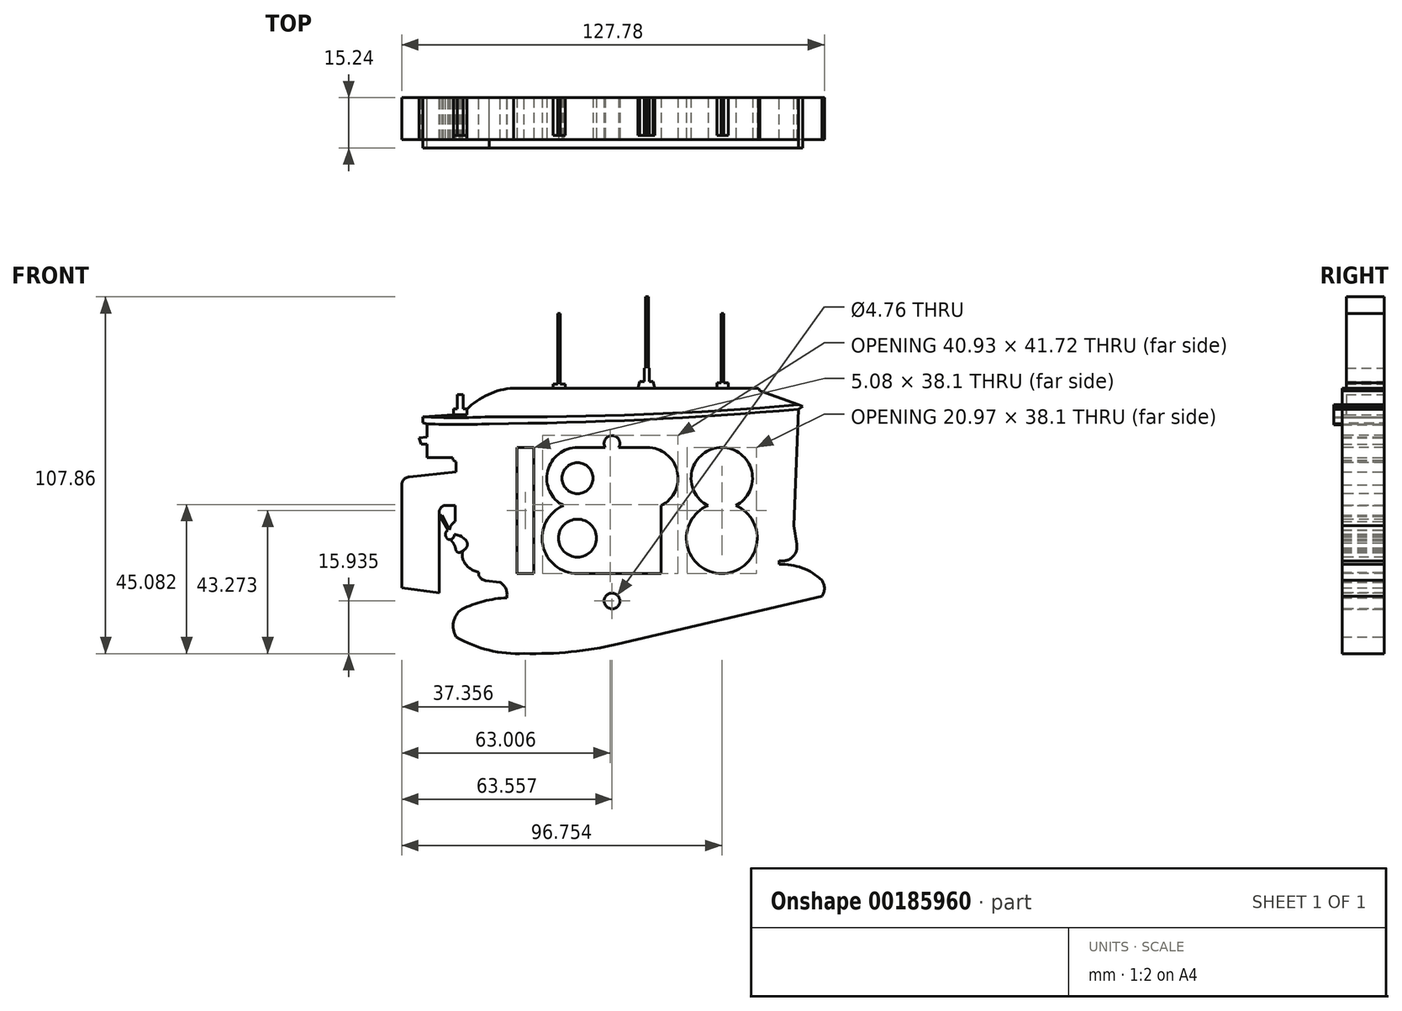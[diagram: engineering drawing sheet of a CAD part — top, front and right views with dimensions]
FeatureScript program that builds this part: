
annotation { "Feature Type Name" : "Feature", "Feature Type Description" : "" }
export const myFeature = defineFeature(function(context is Context, id is Id, definition is map)
    precondition{}
    {
        {
            var Q0;
            Q0=qCreatedBy(makeId("Front.planeOp"),FACE);
            var sketch = newSketch(context, id + "F0", { "sketchPlane" : qUnion([Q0])});
            skLineSegment(sketch, "E0", {"start": v(-48.76, 13.42) * mm, "end": v(-62.86, 11.96) * mm});
            skArc(sketch, "E1", {"start": v(-62.86, 11.96) * mm, "mid": v(-64.46, 11.17) * mm, "end": v(-65.16, 9.53) * mm});
            skLineSegment(sketch, "E2", {"start": v(-65.16, 9.53) * mm, "end": v(-65.16, -21.6) * mm});
            skLineSegment(sketch, "E3", {"start": v(-65.16, -21.6) * mm, "end": v(-53.86, -23.17) * mm});
            skLineSegment(sketch, "E4", {"start": v(-53.86, -23.17) * mm, "end": v(-53.86, 1.02) * mm});
            skArc(sketch, "E5", {"start": v(-52.52, 3.2) * mm, "mid": v(-53.5, 2.3) * mm, "end": v(-53.86, 1.02) * mm});
            skLineSegment(sketch, "E6", {"start": v(-52.52, 3.2) * mm, "end": v(-49.04, 3.2) * mm});
            skLineSegment(sketch, "E7", {"start": v(-48.76, 13.42) * mm, "end": v(-48.76, 16.5) * mm});
            skLineSegment(sketch, "E8", {"start": v(-48.76, 16.5) * mm, "end": v(-49.66, 16.94) * mm});
            skLineSegment(sketch, "E9", {"start": v(-49.66, 16.94) * mm, "end": v(-49.74, 17.72) * mm});
            skLineSegment(sketch, "E10", {"start": v(-49.74, 17.72) * mm, "end": v(-57.46, 17.72) * mm});
            skLineSegment(sketch, "E11", {"start": v(-57.46, 17.72) * mm, "end": v(-57.46, 21.86) * mm});
            skLineSegment(sketch, "E12", {"start": v(-57.46, 21.86) * mm, "end": v(-59.24, 21.86) * mm});
            skLineSegment(sketch, "E13", {"start": v(-59.24, 21.86) * mm, "end": v(-59.95, 23.65) * mm});
            skLineSegment(sketch, "E14", {"start": v(-59.95, 23.65) * mm, "end": v(-57.48, 23.9) * mm});
            skLineSegment(sketch, "E15", {"start": v(-57.48, 23.9) * mm, "end": v(-57.48, 27.94) * mm});
            skLineSegment(sketch, "E16", {"start": v(-57.48, 27.94) * mm, "end": v(-58.72, 28.29) * mm});
            skLineSegment(sketch, "E17", {"start": v(-58.72, 28.29) * mm, "end": v(-58.72, 30.1) * mm});
            skLineSegment(sketch, "E18", {"start": v(-58.72, 30.1) * mm, "end": v(-49.56, 30.65) * mm});
            skLineSegment(sketch, "E19", {"start": v(-49.56, 30.65) * mm, "end": v(-49.56, 32.46) * mm});
            skLineSegment(sketch, "E20", {"start": v(-49.56, 32.46) * mm, "end": v(-48.32, 32.46) * mm});
            skLineSegment(sketch, "E21", {"start": v(-48.32, 32.46) * mm, "end": v(-48.32, 36.74) * mm});
            skLineSegment(sketch, "E22", {"start": v(-48.32, 36.74) * mm, "end": v(-46.61, 36.74) * mm});
            skLineSegment(sketch, "E23", {"start": v(-46.61, 36.74) * mm, "end": v(-46.61, 32.46) * mm});
            skLineSegment(sketch, "E24", {"start": v(-46.61, 32.46) * mm, "end": v(-45.47, 32.46) * mm});
            skLineSegment(sketch, "E25", {"start": v(-45.47, 32.46) * mm, "end": v(-45.47, 32.32) * mm});
            skArc(sketch, "E26", {"start": v(-31.38, 38.73) * mm, "mid": v(-39.02, 36.84) * mm, "end": v(-45.47, 32.32) * mm});
            skLineSegment(sketch, "E27", {"start": v(-31.38, 38.73) * mm, "end": v(42.69, 38.73) * mm});
            skLineSegment(sketch, "E28", {"start": v(42.69, 38.73) * mm, "end": v(43.05, 37.94) * mm});
            skLineSegment(sketch, "E29", {"start": v(43.05, 37.94) * mm, "end": v(56.03, 33.26) * mm});
            skLineSegment(sketch, "E30", {"start": v(56.03, 33.26) * mm, "end": v(54.75, 32.34) * mm});
            skLineSegment(sketch, "E31", {"start": v(54.75, 32.34) * mm, "end": v(53.41, -2.84) * mm});
            skLineSegment(sketch, "E32", {"start": v(53.41, -2.84) * mm, "end": v(54.27, -8.48) * mm});
            skArc(sketch, "E33", {"start": v(48.95, -13.4) * mm, "mid": v(52.92, -12.35) * mm, "end": v(54.27, -8.48) * mm});
            skLineSegment(sketch, "E34", {"start": v(48.95, -13.4) * mm, "end": v(48.95, -14.57) * mm});
            skArc(sketch, "E35", {"start": v(61.84, -19.38) * mm, "mid": v(55.9, -15.63) * mm, "end": v(48.95, -14.57) * mm});
            skArc(sketch, "E36", {"start": v(61.84, -24.22) * mm, "mid": v(62.62, -21.8) * mm, "end": v(61.84, -19.38) * mm});
            skLineSegment(sketch, "E37", {"start": v(61.84, -24.22) * mm, "end": v(0, -38.68) * mm});
            skArc(sketch, "E38", {"start": v(-28.17, -41.47) * mm, "mid": v(-14, -41) * mm, "end": v(0, -38.68) * mm});
            skArc(sketch, "E39", {"start": v(-48.72, -36.43) * mm, "mid": v(-38.82, -40.48) * mm, "end": v(-28.17, -41.47) * mm});
            skArc(sketch, "E40", {"start": v(-47.02, -28.16) * mm, "mid": v(-49.5, -31.96) * mm, "end": v(-48.72, -36.43) * mm});
            skArc(sketch, "E41", {"start": v(-33.4, -24.65) * mm, "mid": v(-40.4, -25.7) * mm, "end": v(-47.02, -28.16) * mm});
            skArc(sketch, "E42", {"start": v(-33.4, -24.65) * mm, "mid": v(-33.66, -21.98) * mm, "end": v(-35.39, -19.93) * mm});
            skLineSegment(sketch, "E43", {"start": v(-35.39, -19.93) * mm, "end": v(-39.85, -19.43) * mm});
            skArc(sketch, "E44", {"start": v(-41.93, -16.91) * mm, "mid": v(-41.4, -18.6) * mm, "end": v(-39.85, -19.43) * mm});
            skArc(sketch, "E45", {"start": v(-46.6, -13.2) * mm, "mid": v(-44.71, -15.62) * mm, "end": v(-41.93, -16.91) * mm});
            skArc(sketch, "E46", {"start": v(-46.6, -10.27) * mm, "mid": v(-46.84, -11.74) * mm, "end": v(-46.6, -13.2) * mm});
            skArc(sketch, "E47", {"start": v(-46.6, -10.27) * mm, "mid": v(-45.82, -8.68) * mm, "end": v(-46.36, -6.99) * mm});
            skLineSegment(sketch, "E48", {"start": v(-49.04, 3.2) * mm, "end": v(-49.04, -1.54) * mm});
            skArc(sketch, "E49", {"start": v(-49.04, -1.54) * mm, "mid": v(-50.85, -5.02) * mm, "end": v(-49.04, -8.5) * mm});
            skArc(sketch, "E50", {"start": v(-49.04, -8.5) * mm, "mid": v(-47.3, -5.02) * mm, "end": v(-49.04, -1.54) * mm});
            skLineSegment(sketch, "E51", {"start": v(-46.36, -6.99) * mm, "end": v(-47.37, -5.75) * mm});
            skArc(sketch, "E52", {"start": v(-50.74, -4.05) * mm, "mid": v(-51.6, -4.53) * mm, "end": v(-51.97, -5.43) * mm});
            skArc(sketch, "E53", {"start": v(-51.97, -5.43) * mm, "mid": v(-51.73, -6.26) * mm, "end": v(-51.19, -6.94) * mm});
            skArc(sketch, "E54", {"start": v(-51.19, -6.94) * mm, "mid": v(-50.77, -7.02) * mm, "end": v(-50.35, -7.02) * mm});
            skArc(sketch, "E55", {"start": v(-50.35, -7.02) * mm, "mid": v(-49.27, -5.37) * mm, "end": v(-50.74, -4.05) * mm});
            skArc(sketch, "E56", {"start": v(-45.65, -7.36) * mm, "mid": v(-47.84, -5.85) * mm, "end": v(-50.48, -5.52) * mm});
            skArc(sketch, "E57", {"start": v(-45.65, -9.55) * mm, "mid": v(-45.29, -8.46) * mm, "end": v(-45.65, -7.36) * mm});
            skArc(sketch, "E58", {"start": v(-47.7, -11) * mm, "mid": v(-46.59, -10.39) * mm, "end": v(-45.65, -9.55) * mm});
            skArc(sketch, "E59", {"start": v(-48.83, -10.03) * mm, "mid": v(-48.44, -10.73) * mm, "end": v(-47.7, -11) * mm});
            skArc(sketch, "E60", {"start": v(-48.83, -10.03) * mm, "mid": v(-49.38, -8.42) * mm, "end": v(-50.35, -7.02) * mm});
            skArc(sketch, "E61", {"start": v(-57.48, 27.94) * mm, "mid": v(-48.1, 27.7) * mm, "end": v(-38.7, 27.94) * mm});
            skArc(sketch, "E62", {"start": v(-38.7, 27.94) * mm, "mid": v(8.07, 29.23) * mm, "end": v(54.75, 32.34) * mm});
            skLineSegment(sketch, "E63", {"start": v(-33.4, -24.65) * mm, "end": v(-33.4, -29.1) * mm});
            skLineSegment(sketch, "E64", {"start": v(-33.4, -29.1) * mm, "end": v(-28.45, -28) * mm});
            skLineSegment(sketch, "E65", {"start": v(-28.45, -28) * mm, "end": v(-28.45, -31.15) * mm});
            skLineSegment(sketch, "E66", {"start": v(-28.45, -31.15) * mm, "end": v(-16.41, -28.65) * mm});
            skLineSegment(sketch, "E67", {"start": v(-16.41, -28.65) * mm, "end": v(-17.59, -27.26) * mm});
            skLineSegment(sketch, "E68", {"start": v(-17.59, -27.26) * mm, "end": v(0, -33.2) * mm});
            skLineSegment(sketch, "E69", {"start": v(0, -33.2) * mm, "end": v(6.99, -31.66) * mm});
            skLineSegment(sketch, "E70", {"start": v(6.99, -31.66) * mm, "end": v(6.99, -12.15) * mm});
            skLineSegment(sketch, "E71", {"start": v(6.99, -12.15) * mm, "end": v(44.04, -6.2) * mm});
            skLineSegment(sketch, "E72", {"start": v(44.04, -6.2) * mm, "end": v(44.04, -23.6) * mm});
            skLineSegment(sketch, "E73", {"start": v(44.04, -23.6) * mm, "end": v(48.95, -22.5) * mm});
            skLineSegment(sketch, "E74", {"start": v(48.95, -22.5) * mm, "end": v(48.95, -14.57) * mm});
            skLineSegment(sketch, "E75", {"start": v(0, -33.2) * mm, "end": v(0, -6.11) * mm});
            skLineSegment(sketch, "E76", {"start": v(0, -6.11) * mm, "end": v(48.68, 1.7) * mm});
            skLineSegment(sketch, "E77", {"start": v(48.68, 1.7) * mm, "end": v(48.95, -13.4) * mm});
            skLineSegment(sketch, "E78", {"start": v(0, -6.11) * mm, "end": v(-5.2, -5.38) * mm});
            skLineSegment(sketch, "E79", {"start": v(-5.2, -5.38) * mm, "end": v(38.9, 1.7) * mm});
            skLineSegment(sketch, "E80", {"start": v(38.9, 1.7) * mm, "end": v(48.68, 1.7) * mm});
            skLineSegment(sketch, "E81", {"start": v(-5.2, -5.38) * mm, "end": v(-5.2, -31.45) * mm});
            skArc(sketch, "E82", {"start": v(-15.78, -17.4) * mm, "mid": v(-8.22, -13.39) * mm, "end": v(-5.2, -5.38) * mm});
            skArc(sketch, "E83", {"start": v(-35.39, -19.93) * mm, "mid": v(-25.56, -18.86) * mm, "end": v(-15.78, -17.4) * mm});
            skArc(sketch, "E84", {"start": v(-58.72, 30.1) * mm, "mid": v(-48.71, 29.82) * mm, "end": v(-38.7, 30.1) * mm});
            skArc(sketch, "E85", {"start": v(-38.7, 30.1) * mm, "mid": v(8.07, 30.8) * mm, "end": v(54.75, 33.72) * mm});
            skLineSegment(sketch, "E86", {"start": v(-19.35, 38.73) * mm, "end": v(-19.35, 39.97) * mm});
            skLineSegment(sketch, "E87", {"start": v(-19.35, 39.97) * mm, "end": v(-15.67, 39.97) * mm});
            skLineSegment(sketch, "E88", {"start": v(-15.67, 39.97) * mm, "end": v(-15.67, 38.73) * mm});
            skLineSegment(sketch, "E89", {"start": v(-18.02, 39.97) * mm, "end": v(-18.02, 61.27) * mm});
            skLineSegment(sketch, "E90", {"start": v(-18.02, 61.27) * mm, "end": v(-17.22, 61.27) * mm});
            skLineSegment(sketch, "E91", {"start": v(-17.22, 61.27) * mm, "end": v(-17.22, 39.97) * mm});
            skLineSegment(sketch, "E92", {"start": v(30.18, 38.73) * mm, "end": v(30.18, 40.4) * mm});
            skLineSegment(sketch, "E93", {"start": v(30.18, 40.4) * mm, "end": v(33.56, 40.4) * mm});
            skLineSegment(sketch, "E94", {"start": v(33.56, 40.4) * mm, "end": v(33.56, 38.73) * mm});
            skLineSegment(sketch, "E95", {"start": v(31.4, 40.4) * mm, "end": v(31.4, 61.27) * mm});
            skLineSegment(sketch, "E96", {"start": v(31.4, 61.27) * mm, "end": v(32.2, 61.27) * mm});
            skLineSegment(sketch, "E97", {"start": v(32.2, 61.27) * mm, "end": v(32.2, 40.4) * mm});
            skLineSegment(sketch, "E98", {"start": v(6.24, 38.73) * mm, "end": v(6.79, 40.79) * mm});
            skLineSegment(sketch, "E99", {"start": v(6.79, 40.79) * mm, "end": v(8.11, 40.79) * mm});
            skLineSegment(sketch, "E100", {"start": v(8.11, 40.79) * mm, "end": v(8.11, 44.74) * mm});
            skLineSegment(sketch, "E101", {"start": v(8.11, 44.74) * mm, "end": v(9.64, 44.74) * mm});
            skLineSegment(sketch, "E102", {"start": v(9.64, 44.74) * mm, "end": v(9.64, 40.79) * mm});
            skLineSegment(sketch, "E103", {"start": v(9.64, 40.79) * mm, "end": v(10.8, 40.79) * mm});
            skLineSegment(sketch, "E104", {"start": v(10.8, 40.79) * mm, "end": v(11.36, 38.73) * mm});
            skLineSegment(sketch, "E105", {"start": v(8.57, 44.74) * mm, "end": v(8.57, 66.33) * mm});
            skLineSegment(sketch, "E106", {"start": v(8.57, 66.33) * mm, "end": v(9.38, 66.33) * mm});
            skLineSegment(sketch, "E107", {"start": v(9.38, 66.33) * mm, "end": v(9.38, 44.74) * mm});
            skLineSegment(sketch, "E108", {"start": v(6.99, -31.66) * mm, "end": v(44.04, -23.6) * mm});
            skArc(sketch, "E109", {"start": v(-28.12, -36.29) * mm, "mid": v(-13.98, -35.5) * mm, "end": v(0, -33.2) * mm});
            skArc(sketch, "E110", {"start": v(-45.38, -33.2) * mm, "mid": v(-36.97, -35.96) * mm, "end": v(-28.12, -36.29) * mm});
            skArc(sketch, "E111", {"start": v(-47.02, -28.16) * mm, "mid": v(-46.99, -30.94) * mm, "end": v(-45.38, -33.2) * mm});
            skLineSegment(sketch, "E112", {"start": v(-49.56, 30.65) * mm, "end": v(-45.47, 30.65) * mm});
            skLineSegment(sketch, "E113", {"start": v(-45.47, 30.65) * mm, "end": v(-45.47, 32.32) * mm});
            skLineSegment(sketch, "E114", {"start": v(-51.2, -4.22) * mm, "end": v(-53.6, -0.05) * mm});
            skLineSegment(sketch, "E115", {"start": v(-53.6, -0.05) * mm, "end": v(-52.96, 0.32) * mm});
            skLineSegment(sketch, "E116", {"start": v(-52.96, 0.32) * mm, "end": v(-50.74, -4.05) * mm});
            skSolve(sketch);
        }
        {
            var Q0;
            Q0=makeQuery(id+"F0.imprint","IMPRINT",FACE,{"disambiguationData":[TD([[makeQuery(id+"F0.imprint","IMPRINT",EDGE,{"derivedFrom":sQuery(id+"F0.wireOp",EDGE,"E0")}),1.0]])]});
            var Q1;
            {var subQ5=sQuery(id+"F0.wireOp",EDGE,"E50");var subQ7=makeQuery(id+"F0.imprint","INTERSECT",VERTEX,{"derivedFrom":[subQ5,sQuery(id+"F0.wireOp",EDGE,"E51")]});Q1=makeQuery(id+"F0.imprint","IMPRINT",FACE,{"disambiguationData":[TD([[makeQuery(id+"F0.imprint","IMPRINT",EDGE,{"disambiguationData":[TD([[subQ7,1.0]])],"derivedFrom":subQ5}),1.0]])]});}
            var Q2;
            {var subQ0=sQuery(id+"F0.wireOp",EDGE,"E53");Q2=makeQuery(id+"F0.imprint","IMPRINT",FACE,{"disambiguationData":[TD([[makeQuery(id+"F0.imprint","IMPRINT",EDGE,{"derivedFrom":subQ0}),1.0]])]});}
            var Q3;
            {var subQ1=sQuery(id+"F0.wireOp",EDGE,"E49");var subQ3=makeQuery(id+"F0.imprint","INTERSECT",VERTEX,{"derivedFrom":[subQ1,sQuery(id+"F0.wireOp",EDGE,"JAnZBrHo-FBBG-eloX-0JCn-rR0iuovSbzPm")]});Q3=makeQuery(id+"F0.imprint","IMPRINT",FACE,{"disambiguationData":[TD([[makeQuery(id+"F0.imprint","IMPRINT",EDGE,{"disambiguationData":[TD([[subQ3,1.0]])],"derivedFrom":subQ1}),1.0]])]});}
            var Q4;
            Q4=makeQuery(id+"F0.imprint","IMPRINT",FACE,{"disambiguationData":[TD([[makeQuery(id+"F0.imprint","IMPRINT",EDGE,{"derivedFrom":sQuery(id+"F0.wireOp",EDGE,"E41")}),1.0]])]});
            var Q5;
            Q5=makeQuery(id+"F0.imprint","IMPRINT",FACE,{"disambiguationData":[TD([[makeQuery(id+"F0.imprint","IMPRINT",EDGE,{"derivedFrom":sQuery(id+"F0.wireOp",EDGE,"E35")}),1.0]])]});
            var Q6;
            Q6=makeQuery(id+"F0.imprint","IMPRINT",FACE,{"disambiguationData":[TD([[makeQuery(id+"F0.imprint","IMPRINT",EDGE,{"derivedFrom":sQuery(id+"F0.wireOp",EDGE,"E42")}),-1.0]])]});
            var Q7;
            Q7=makeQuery(id+"F0.imprint","IMPRINT",FACE,{"disambiguationData":[TD([[makeQuery(id+"F0.imprint","IMPRINT",EDGE,{"derivedFrom":sQuery(id+"F0.wireOp",EDGE,"E70")}),-1.0]])]});
            var Q8;
            Q8=makeQuery(id+"F0.imprint","IMPRINT",FACE,{"disambiguationData":[TD([[makeQuery(id+"F0.imprint","IMPRINT",EDGE,{"derivedFrom":sQuery(id+"F0.wireOp",EDGE,"E18")}),-1.0]])]});
            var Q9;
            Q9=makeQuery(id+"F0.imprint","IMPRINT",FACE,{"disambiguationData":[TD([[makeQuery(id+"F0.imprint","IMPRINT",EDGE,{"derivedFrom":sQuery(id+"F0.wireOp",EDGE,"E34")}),-1.0]])]});
            var Q10;
            Q10=makeQuery(id+"F0.imprint","IMPRINT",FACE,{"disambiguationData":[TD([[makeQuery(id+"F0.imprint","IMPRINT",EDGE,{"derivedFrom":sQuery(id+"F0.wireOp",EDGE,"E76")}),1.0]])]});
            var Q11;
            {var subQ0=sQuery(id+"F0.wireOp",EDGE,"E75");Q11=makeQuery(id+"F0.imprint","IMPRINT",FACE,{"disambiguationData":[TD([[makeQuery(id+"F0.imprint","IMPRINT",EDGE,{"derivedFrom":subQ0}),1.0]])]});}
            var Q12;
            {var subQ0=sQuery(id+"F0.wireOp",EDGE,"E55");var subQ4=makeQuery(id+"F0.imprint","INTERSECT",VERTEX,{"derivedFrom":[subQ0,sQuery(id+"F0.wireOp",EDGE,"E56")]});Q12=makeQuery(id+"F0.imprint","IMPRINT",FACE,{"disambiguationData":[TD([[makeQuery(id+"F0.imprint","IMPRINT",EDGE,{"disambiguationData":[TD([[subQ4,1.0]])],"derivedFrom":subQ0}),1.0]])]});}
            var Q13;
            {var subQ2=sQuery(id+"F0.wireOp",EDGE,"E114");Q13=makeQuery(id+"F0.imprint","IMPRINT",FACE,{"disambiguationData":[TD([[makeQuery(id+"F0.imprint","IMPRINT",EDGE,{"derivedFrom":subQ2}),-1.0]])]});}
            var Q14;
            {var subQ2=sQuery(id+"F0.wireOp",EDGE,"E49");var subQ6=sQuery(id+"F0.wireOp",EDGE,"E50");var subQ7=makeQuery(id+"F0.imprint","INTERSECT",VERTEX,{"derivedFrom":[subQ2,subQ6]});Q14=makeQuery(id+"F0.imprint","IMPRINT",FACE,{"disambiguationData":[TD([[makeQuery(id+"F0.imprint","IMPRINT",EDGE,{"disambiguationData":[TD([[subQ7,1.0]])],"derivedFrom":subQ2}),1.0]])]});}
            var Q15;
            {var subQ8=sQuery(id+"F0.wireOp",EDGE,"E47");Q15=makeQuery(id+"F0.imprint","IMPRINT",FACE,{"disambiguationData":[TD([[makeQuery(id+"F0.imprint","IMPRINT",EDGE,{"derivedFrom":subQ8}),1.0]])]});}
            var Q16;
            {var subQ4=sQuery(id+"F0.wireOp",EDGE,"E47");Q16=makeQuery(id+"F0.imprint","IMPRINT",FACE,{"disambiguationData":[TD([[makeQuery(id+"F0.imprint","IMPRINT",EDGE,{"derivedFrom":subQ4}),-1.0]])]});}
            var Q17;
            {var subQ0=sQuery(id+"F0.wireOp",EDGE,"E51");var subQ1=sQuery(id+"F0.wireOp",EDGE,"E50");var subQ2=makeQuery(id+"F0.imprint","INTERSECT",VERTEX,{"derivedFrom":[subQ1,subQ0]});Q17=makeQuery(id+"F0.imprint","IMPRINT",FACE,{"disambiguationData":[TD([[makeQuery(id+"F0.imprint","IMPRINT",EDGE,{"disambiguationData":[TD([[subQ2,1.0]])],"derivedFrom":subQ1}),-1.0]])]});}
            extrude(context, id + "F1", {"entities" : qUnion([Q0, Q1, Q2, Q3, Q4, Q5, Q6, Q7, Q8, Q9, Q10, Q11, Q12, Q13, Q14, Q15, Q16, Q17]), "depth" : 12.7 * mm});
        }
        {
            var Q0;
            {var subQ5=sQuery(id+"F0.wireOp",EDGE,"E47");Q0=makeQuery(id+"F0.imprint","IMPRINT",FACE,{"disambiguationData":[TD([[makeQuery(id+"F0.imprint","IMPRINT",EDGE,{"derivedFrom":subQ5}),1.0]])]});}
            var Q1;
            {var subQ3=sQuery(id+"F0.wireOp",EDGE,"E50");var subQ6=sQuery(id+"F0.wireOp",EDGE,"E49");var subQ8=makeQuery(id+"F0.imprint","INTERSECT",VERTEX,{"derivedFrom":[subQ6,subQ3]});Q1=makeQuery(id+"F0.imprint","IMPRINT",FACE,{"disambiguationData":[TD([[makeQuery(id+"F0.imprint","IMPRINT",EDGE,{"disambiguationData":[TD([[subQ8,1.0]])],"derivedFrom":subQ6}),1.0]])]});}
            var Q2;
            {var subQ0=sQuery(id+"F0.wireOp",EDGE,"wI7tyHVv-ab6v-So0j-KQO8-YM4SJzSUTnYV");Q2=makeQuery(id+"F0.imprint","IMPRINT",FACE,{"disambiguationData":[TD([[makeQuery(id+"F0.imprint","IMPRINT",EDGE,{"derivedFrom":subQ0}),1.0]])]});}
            var Q3;
            {var subQ1=sQuery(id+"F0.wireOp",EDGE,"E49");var subQ3=sQuery(id+"F0.wireOp",EDGE,"JAnZBrHo-FBBG-eloX-0JCn-rR0iuovSbzPm");var subQ4=makeQuery(id+"F0.imprint","INTERSECT",VERTEX,{"derivedFrom":[subQ1,subQ3]});Q3=makeQuery(id+"F0.imprint","IMPRINT",FACE,{"disambiguationData":[TD([[makeQuery(id+"F0.imprint","IMPRINT",EDGE,{"disambiguationData":[TD([[subQ4,1.0]])],"derivedFrom":subQ3}),1.0]])]});}
            var Q4;
            {var subQ4=sQuery(id+"F0.wireOp",EDGE,"E47");Q4=makeQuery(id+"F0.imprint","IMPRINT",FACE,{"disambiguationData":[TD([[makeQuery(id+"F0.imprint","IMPRINT",EDGE,{"derivedFrom":subQ4}),-1.0]])]});}
            var Q5;
            {var subQ0=sQuery(id+"F0.wireOp",EDGE,"E51");var subQ1=sQuery(id+"F0.wireOp",EDGE,"E50");var subQ2=makeQuery(id+"F0.imprint","INTERSECT",VERTEX,{"derivedFrom":[subQ1,subQ0]});Q5=makeQuery(id+"F0.imprint","IMPRINT",FACE,{"disambiguationData":[TD([[makeQuery(id+"F0.imprint","IMPRINT",EDGE,{"disambiguationData":[TD([[subQ2,1.0]])],"derivedFrom":subQ1}),-1.0]])]});}
            var Q6;
            {var subQ0=sQuery(id+"F0.wireOp",EDGE,"E60");var subQ1=sQuery(id+"F0.wireOp",EDGE,"E49");var subQ3=makeQuery(id+"F0.imprint","INTERSECT",VERTEX,{"derivedFrom":[subQ1,subQ0]});Q6=makeQuery(id+"F0.imprint","IMPRINT",FACE,{"disambiguationData":[TD([[makeQuery(id+"F0.imprint","IMPRINT",EDGE,{"disambiguationData":[TD([[subQ3,1.0]])],"derivedFrom":subQ1}),1.0]])]});}
            extrude(context, id + "F2", {"entities" : qUnion([Q0, Q1, Q2, Q3, Q4, Q5, Q6]), "depth" : 12.7 * mm});
        }
        {
            var Q0;
            Q0=makeQuery(id+"F0.imprint","IMPRINT",FACE,{"disambiguationData":[TD([[makeQuery(id+"F0.imprint","IMPRINT",EDGE,{"derivedFrom":sQuery(id+"F0.wireOp",EDGE,"E16")}),-1.0]])]});
            extrude(context, id + "F3", {"entities" : qUnion([Q0]), "depth" : 15.24 * mm});
        }
        {
            var Q0;
            Q0=makeQuery(id+"F0.imprint","IMPRINT",FACE,{"disambiguationData":[TD([[makeQuery(id+"F0.imprint","IMPRINT",EDGE,{"derivedFrom":sQuery(id+"F0.wireOp",EDGE,"E19")}),-1.0]])]});
            var Q1;
            {var subQ3=sQuery(id+"F0.wireOp",EDGE,"E86");Q1=makeQuery(id+"F0.imprint","IMPRINT",FACE,{"disambiguationData":[TD([[makeQuery(id+"F0.imprint","IMPRINT",EDGE,{"derivedFrom":subQ3}),-1.0]])]});}
            var Q2;
            {var subQ1=sQuery(id+"F0.wireOp",EDGE,"E98");Q2=makeQuery(id+"F0.imprint","IMPRINT",FACE,{"disambiguationData":[TD([[makeQuery(id+"F0.imprint","IMPRINT",EDGE,{"derivedFrom":subQ1}),-1.0]])]});}
            var Q3;
            {var subQ0=sQuery(id+"F0.wireOp",EDGE,"E95");Q3=makeQuery(id+"F0.imprint","IMPRINT",FACE,{"disambiguationData":[TD([[makeQuery(id+"F0.imprint","IMPRINT",EDGE,{"derivedFrom":subQ0}),-1.0]])]});}
            var Q4;
            {var subQ3=sQuery(id+"F0.wireOp",EDGE,"E92");Q4=makeQuery(id+"F0.imprint","IMPRINT",FACE,{"disambiguationData":[TD([[makeQuery(id+"F0.imprint","IMPRINT",EDGE,{"derivedFrom":subQ3}),-1.0]])]});}
            var Q5;
            {var subQ0=sQuery(id+"F0.wireOp",EDGE,"E89");Q5=makeQuery(id+"F0.imprint","IMPRINT",FACE,{"disambiguationData":[TD([[makeQuery(id+"F0.imprint","IMPRINT",EDGE,{"derivedFrom":subQ0}),-1.0]])]});}
            var Q6;
            {var subQ0=sQuery(id+"F0.wireOp",EDGE,"E105");Q6=makeQuery(id+"F0.imprint","IMPRINT",FACE,{"disambiguationData":[TD([[makeQuery(id+"F0.imprint","IMPRINT",EDGE,{"derivedFrom":subQ0}),-1.0]])]});}
            extrude(context, id + "F4", {"entities" : qUnion([Q0, Q1, Q2, Q3, Q4, Q5, Q6]), "operationType" : NewBodyOperationType.ADD, "depth" : 11.43 * mm});
        }
        {
            var Q0;
            Q0=makeQuery(id+"F2.opExtrude","SWEPT_BODY",BODY,{"disambiguationData":[OSD([sQuery(id+"F0.wireOp",EDGE,"E49"),sQuery(id+"F0.wireOp",EDGE,"E50"),sQuery(id+"F0.wireOp",EDGE,"E51"),sQuery(id+"F0.wireOp",EDGE,"E55"),sQuery(id+"F0.wireOp",EDGE,"E56"),sQuery(id+"F0.wireOp",EDGE,"E57"),sQuery(id+"F0.wireOp",EDGE,"E58"),sQuery(id+"F0.wireOp",EDGE,"E59"),sQuery(id+"F0.wireOp",EDGE,"E60")])]});
            var Q1;
            Q1=makeQuery(id+"F1.opExtrude","SWEPT_BODY",BODY,{"disambiguationData":[OSD([sQuery(id+"F0.wireOp",EDGE,"E18"),sQuery(id+"F0.wireOp",EDGE,"E26"),sQuery(id+"F0.wireOp",EDGE,"E27"),sQuery(id+"F0.wireOp",EDGE,"E28"),sQuery(id+"F0.wireOp",EDGE,"E29"),sQuery(id+"F0.wireOp",EDGE,"E84"),sQuery(id+"F0.wireOp",EDGE,"E85"),sQuery(id+"F0.wireOp",EDGE,"E112"),sQuery(id+"F0.wireOp",EDGE,"E113")])]});
            booleanBodies(context, id + "F5", {"operationType" : BooleanOperationType.UNION, "tools" : qUnion([Q0, Q1])});
        }
        {
            var Q0;
            {var subQ0=sQuery(id+"F0.wireOp",EDGE,"E58");var subQ1=sQuery(id+"F0.wireOp",EDGE,"E57");var subQ2=sQuery(id+"F0.wireOp",EDGE,"E56");var subQ3=sQuery(id+"F0.wireOp",EDGE,"E55");var subQ4=sQuery(id+"F0.wireOp",EDGE,"E51");var subQ5=sQuery(id+"F0.wireOp",EDGE,"E50");var subQ6=sQuery(id+"F0.wireOp",EDGE,"E49");Q0=makeQuery(id+"F5.opBoolean","MERGE",FACE,{"derivedFrom":[makeQuery(id+"F1.opExtrude","CAP_FACE",FACE,{"disambiguationData":[OSD([sQuery(id+"F0.wireOp",EDGE,"E0"),sQuery(id+"F0.wireOp",EDGE,"E1"),sQuery(id+"F0.wireOp",EDGE,"E2"),sQuery(id+"F0.wireOp",EDGE,"E3"),sQuery(id+"F0.wireOp",EDGE,"E4"),sQuery(id+"F0.wireOp",EDGE,"E5"),sQuery(id+"F0.wireOp",EDGE,"E6"),sQuery(id+"F0.wireOp",EDGE,"E7"),sQuery(id+"F0.wireOp",EDGE,"E8"),sQuery(id+"F0.wireOp",EDGE,"E9"),sQuery(id+"F0.wireOp",EDGE,"E10"),sQuery(id+"F0.wireOp",EDGE,"E11"),sQuery(id+"F0.wireOp",EDGE,"E12"),sQuery(id+"F0.wireOp",EDGE,"E13"),sQuery(id+"F0.wireOp",EDGE,"E14"),sQuery(id+"F0.wireOp",EDGE,"E15"),sQuery(id+"F0.wireOp",EDGE,"E31"),sQuery(id+"F0.wireOp",EDGE,"E32"),sQuery(id+"F0.wireOp",EDGE,"E33"),sQuery(id+"F0.wireOp",EDGE,"E34"),sQuery(id+"F0.wireOp",EDGE,"E35"),sQuery(id+"F0.wireOp",EDGE,"E36"),sQuery(id+"F0.wireOp",EDGE,"E37"),sQuery(id+"F0.wireOp",EDGE,"E38"),sQuery(id+"F0.wireOp",EDGE,"E39"),sQuery(id+"F0.wireOp",EDGE,"E40"),sQuery(id+"F0.wireOp",EDGE,"E41"),sQuery(id+"F0.wireOp",EDGE,"E42"),sQuery(id+"F0.wireOp",EDGE,"E43"),sQuery(id+"F0.wireOp",EDGE,"E44"),sQuery(id+"F0.wireOp",EDGE,"E45"),sQuery(id+"F0.wireOp",EDGE,"E46"),sQuery(id+"F0.wireOp",EDGE,"E48"),subQ6,subQ5,subQ4,sQuery(id+"F0.wireOp",EDGE,"JAnZBrHo-FBBG-eloX-0JCn-rR0iuovSbzPm"),sQuery(id+"F0.wireOp",EDGE,"E52"),sQuery(id+"F0.wireOp",EDGE,"E53"),sQuery(id+"F0.wireOp",EDGE,"E54"),subQ3,subQ2,subQ1,subQ0,sQuery(id+"F0.wireOp",EDGE,"E61"),sQuery(id+"F0.wireOp",EDGE,"E62")])],"isStart":false}),makeQuery(id+"F2.opExtrude","CAP_FACE",FACE,{"disambiguationData":[OSD([subQ6,subQ5,subQ4,subQ3,subQ2,subQ1,subQ0,sQuery(id+"F0.wireOp",EDGE,"E59"),sQuery(id+"F0.wireOp",EDGE,"E60")])],"isStart":false})]});}
            var sketch = newSketch(context, id + "F6", { "sketchPlane" : qUnion([Q0])});
            skLineSegment(sketch, "E117.bottom", {"start": v(-30.34, 20.8) * mm, "end": v(-25.26, 20.8) * mm});
            skLineSegment(sketch, "E117.top", {"start": v(-30.34, -17.3) * mm, "end": v(-25.26, -17.3) * mm});
            skLineSegment(sketch, "E117.left", {"start": v(-30.34, 20.8) * mm, "end": v(-30.34, -17.3) * mm});
            skLineSegment(sketch, "E117.right", {"start": v(-25.26, 20.8) * mm, "end": v(-25.26, -17.3) * mm});
            skLineSegment(sketch, "E118", {"start": v(-30.34, 20.8) * mm, "end": v(35.18, 20.8) * mm});
            skLineSegment(sketch, "E119", {"start": v(-30.34, -17.3) * mm, "end": v(35.18, -17.3) * mm});
            skCircle(sketch, "E120", {"center": v(9.07, 11.51) * mm, "radius": 9.28 * mm});
            skLineSegment(sketch, "E121.bottom", {"start": v(18.35, 11.51) * mm, "end": v(13.27, 11.51) * mm});
            skLineSegment(sketch, "E121.top", {"start": v(18.35, -17.3) * mm, "end": v(13.27, -17.3) * mm});
            skLineSegment(sketch, "E121.left", {"start": v(18.35, 11.51) * mm, "end": v(18.35, -17.3) * mm});
            skLineSegment(sketch, "E121.right", {"start": v(13.27, 11.51) * mm, "end": v(13.27, -17.3) * mm});
            skCircle(sketch, "E122", {"center": v(9.07, 11.51) * mm, "radius": 4.2 * mm});
            skLineSegment(sketch, "E123", {"start": v(9.07, 11.51) * mm, "end": v(13.27, 11.51) * mm});
            skLineSegment(sketch, "E124", {"start": v(-12.02, 20.8) * mm, "end": v(-12.02, -17.3) * mm});
            skCircle(sketch, "E125", {"center": v(-12.02, 11.51) * mm, "radius": 9.28 * mm});
            skLineSegment(sketch, "E126", {"start": v(-12.02, 11.51) * mm, "end": v(-12.02, -17.3) * mm});
            skCircle(sketch, "E127", {"center": v(-12.02, -6.6) * mm, "radius": 10.7 * mm});
            skCircle(sketch, "E128", {"center": v(-12.02, -6.6) * mm, "radius": 5.73 * mm});
            skCircle(sketch, "E129", {"center": v(-12.02, 11.51) * mm, "radius": 4.68 * mm});
            skLineSegment(sketch, "E130", {"start": v(31.6, 20.8) * mm, "end": v(31.6, -17.3) * mm});
            skCircle(sketch, "E131", {"center": v(31.6, 11.51) * mm, "radius": 9.28 * mm});
            skPoint(sketch, "E131.centerSnap0", {"position": v(15.81, 11.51) * mm});
            skCircle(sketch, "E132", {"center": v(31.6, -6.6) * mm, "radius": 10.7 * mm});
            skCircle(sketch, "E133", {"center": v(31.6, -6.6) * mm, "radius": 5.82 * mm});
            skCircle(sketch, "E134", {"center": v(31.6, 11.51) * mm, "radius": 5.02 * mm});
            skSolve(sketch);
        }
        {
            var Q0;
            {var subQ0=sQuery(id+"F6.wireOp",EDGE,"E117.left");Q0=makeQuery(id+"F6.imprint","IMPRINT",FACE,{"disambiguationData":[TD([[makeQuery(id+"F6.imprint","IMPRINT",EDGE,{"derivedFrom":subQ0}),1.0]])]});}
            var Q1;
            {var subQ3=sQuery(id+"F6.wireOp",EDGE,"E126");var subQ5=sQuery(id+"F6.wireOp",EDGE,"E129");var subQ6=makeQuery(id+"F6.imprint","INTERSECT",VERTEX,{"derivedFrom":[subQ3,subQ5]});Q1=makeQuery(id+"F6.imprint","IMPRINT",FACE,{"disambiguationData":[TD([[makeQuery(id+"F6.imprint","IMPRINT",EDGE,{"disambiguationData":[TD([[subQ6,-1.0]])],"derivedFrom":subQ3}),-1.0]])]});}
            var Q2;
            {var subQ3=sQuery(id+"F6.wireOp",EDGE,"E126");var subQ7=sQuery(id+"F6.wireOp",EDGE,"E129");var subQ9=makeQuery(id+"F6.imprint","INTERSECT",VERTEX,{"derivedFrom":[subQ3,subQ7]});Q2=makeQuery(id+"F6.imprint","IMPRINT",FACE,{"disambiguationData":[TD([[makeQuery(id+"F6.imprint","IMPRINT",EDGE,{"disambiguationData":[TD([[subQ9,-1.0]])],"derivedFrom":subQ3}),1.0]])]});}
            var Q3;
            {var subQ0=sQuery(id+"F6.wireOp",EDGE,"E126");var subQ1=sQuery(id+"F6.wireOp",EDGE,"E125");var subQ2=makeQuery(id+"F6.imprint","INTERSECT",VERTEX,{"derivedFrom":[subQ1,subQ0]});Q3=makeQuery(id+"F6.imprint","IMPRINT",FACE,{"disambiguationData":[TD([[makeQuery(id+"F6.imprint","IMPRINT",EDGE,{"disambiguationData":[TD([[subQ2,-1.0]])],"derivedFrom":subQ1}),1.0]])]});}
            var Q4;
            {var subQ0=sQuery(id+"F6.wireOp",EDGE,"E127");var subQ1=sQuery(id+"F6.wireOp",EDGE,"E125");var subQ2=makeQuery(id+"F6.imprint","INTERSECT",VERTEX,{"disambiguationData":[OD(0.0)],"derivedFrom":[subQ1,subQ0]});Q4=makeQuery(id+"F6.imprint","IMPRINT",FACE,{"disambiguationData":[TD([[makeQuery(id+"F6.imprint","IMPRINT",EDGE,{"disambiguationData":[TD([[subQ2,-1.0]])],"derivedFrom":subQ1}),1.0]])]});}
            var Q5;
            {var subQ0=sQuery(id+"F6.wireOp",EDGE,"E127");var subQ3=sQuery(id+"F6.wireOp",EDGE,"E125");var subQ4=makeQuery(id+"F6.imprint","INTERSECT",VERTEX,{"disambiguationData":[OD(0.0)],"derivedFrom":[subQ3,subQ0]});Q5=makeQuery(id+"F6.imprint","IMPRINT",FACE,{"disambiguationData":[TD([[makeQuery(id+"F6.imprint","IMPRINT",EDGE,{"disambiguationData":[TD([[subQ4,-1.0]])],"derivedFrom":subQ3}),-1.0]])]});}
            var Q6;
            {var subQ1=sQuery(id+"F6.wireOp",EDGE,"E126");var subQ6=sQuery(id+"F6.wireOp",EDGE,"E125");var subQ8=makeQuery(id+"F6.imprint","INTERSECT",VERTEX,{"derivedFrom":[subQ6,subQ1]});Q6=makeQuery(id+"F6.imprint","IMPRINT",FACE,{"disambiguationData":[TD([[makeQuery(id+"F6.imprint","IMPRINT",EDGE,{"disambiguationData":[TD([[subQ8,-1.0]])],"derivedFrom":subQ6}),-1.0]])]});}
            var Q7;
            {var subQ2=sQuery(id+"F6.wireOp",EDGE,"E121.bottom");Q7=makeQuery(id+"F6.imprint","IMPRINT",FACE,{"disambiguationData":[TD([[makeQuery(id+"F6.imprint","IMPRINT",EDGE,{"derivedFrom":subQ2}),-1.0]])]});}
            var Q8;
            {var subQ0=sQuery(id+"F6.wireOp",EDGE,"E121.bottom");Q8=makeQuery(id+"F6.imprint","IMPRINT",FACE,{"disambiguationData":[TD([[makeQuery(id+"F6.imprint","IMPRINT",EDGE,{"derivedFrom":subQ0}),1.0]])]});}
            var Q9;
            {var subQ4=sQuery(id+"F6.wireOp",EDGE,"E121.top");Q9=makeQuery(id+"F6.imprint","IMPRINT",FACE,{"disambiguationData":[TD([[makeQuery(id+"F6.imprint","IMPRINT",EDGE,{"derivedFrom":subQ4}),-1.0]])]});}
            var Q10;
            {var subQ1=sQuery(id+"F6.wireOp",EDGE,"E130");var subQ5=sQuery(id+"F6.wireOp",EDGE,"E134");var subQ7=makeQuery(id+"F6.imprint","INTERSECT",VERTEX,{"disambiguationData":[OD(1.0)],"derivedFrom":[subQ1,subQ5]});Q10=makeQuery(id+"F6.imprint","IMPRINT",FACE,{"disambiguationData":[TD([[makeQuery(id+"F6.imprint","IMPRINT",EDGE,{"disambiguationData":[TD([[subQ7,-1.0]])],"derivedFrom":subQ1}),-1.0]])]});}
            var Q11;
            {var subQ1=sQuery(id+"F6.wireOp",EDGE,"E130");var subQ6=sQuery(id+"F6.wireOp",EDGE,"E134");var subQ8=makeQuery(id+"F6.imprint","INTERSECT",VERTEX,{"disambiguationData":[OD(1.0)],"derivedFrom":[subQ1,subQ6]});Q11=makeQuery(id+"F6.imprint","IMPRINT",FACE,{"disambiguationData":[TD([[makeQuery(id+"F6.imprint","IMPRINT",EDGE,{"disambiguationData":[TD([[subQ8,-1.0]])],"derivedFrom":subQ1}),1.0]])]});}
            var Q12;
            {var subQ0=sQuery(id+"F6.wireOp",EDGE,"E132");var subQ1=sQuery(id+"F6.wireOp",EDGE,"E130");var subQ2=makeQuery(id+"F6.imprint","INTERSECT",VERTEX,{"derivedFrom":[subQ1,subQ0]});Q12=makeQuery(id+"F6.imprint","IMPRINT",FACE,{"disambiguationData":[TD([[makeQuery(id+"F6.imprint","IMPRINT",EDGE,{"disambiguationData":[TD([[subQ2,-1.0]])],"derivedFrom":subQ1}),1.0]])]});}
            var Q13;
            {var subQ0=sQuery(id+"F6.wireOp",EDGE,"E132");var subQ1=sQuery(id+"F6.wireOp",EDGE,"E130");var subQ2=makeQuery(id+"F6.imprint","INTERSECT",VERTEX,{"derivedFrom":[subQ1,subQ0]});Q13=makeQuery(id+"F6.imprint","IMPRINT",FACE,{"disambiguationData":[TD([[makeQuery(id+"F6.imprint","IMPRINT",EDGE,{"disambiguationData":[TD([[subQ2,-1.0]])],"derivedFrom":subQ1}),-1.0]])]});}
            var Q14;
            {var subQ0=sQuery(id+"F6.wireOp",EDGE,"E131");var subQ1=sQuery(id+"F6.wireOp",EDGE,"E130");var subQ2=makeQuery(id+"F6.imprint","INTERSECT",VERTEX,{"derivedFrom":[subQ1,subQ0]});Q14=makeQuery(id+"F6.imprint","IMPRINT",FACE,{"disambiguationData":[TD([[makeQuery(id+"F6.imprint","IMPRINT",EDGE,{"disambiguationData":[TD([[subQ2,-1.0]])],"derivedFrom":subQ1}),-1.0]])]});}
            var Q15;
            {var subQ0=sQuery(id+"F6.wireOp",EDGE,"E131");var subQ1=sQuery(id+"F6.wireOp",EDGE,"E130");var subQ2=makeQuery(id+"F6.imprint","INTERSECT",VERTEX,{"derivedFrom":[subQ1,subQ0]});Q15=makeQuery(id+"F6.imprint","IMPRINT",FACE,{"disambiguationData":[TD([[makeQuery(id+"F6.imprint","IMPRINT",EDGE,{"disambiguationData":[TD([[subQ2,-1.0]])],"derivedFrom":subQ1}),1.0]])]});}
            var Q16;
            {var subQ0=sQuery(id+"F6.wireOp",EDGE,"E126");var subQ1=sQuery(id+"F6.wireOp",EDGE,"E124");var subQ2=makeQuery(id+"F6.imprint","INTERSECT",VERTEX,{"derivedFrom":[subQ1,subQ0]});Q16=makeQuery(id+"F6.imprint","IMPRINT",FACE,{"disambiguationData":[TD([[makeQuery(id+"F6.imprint","IMPRINT",EDGE,{"disambiguationData":[TD([[subQ2,1.0]])],"derivedFrom":subQ1}),-1.0]])]});}
            var Q17;
            {var subQ0=sQuery(id+"F6.wireOp",EDGE,"E126");var subQ1=sQuery(id+"F6.wireOp",EDGE,"E124");var subQ2=makeQuery(id+"F6.imprint","INTERSECT",VERTEX,{"derivedFrom":[subQ1,subQ0]});Q17=makeQuery(id+"F6.imprint","IMPRINT",FACE,{"disambiguationData":[TD([[makeQuery(id+"F6.imprint","IMPRINT",EDGE,{"disambiguationData":[TD([[subQ2,1.0]])],"derivedFrom":subQ1}),1.0]])]});}
            var Q18;
            {var subQ0=sQuery(id+"F6.wireOp",EDGE,"E128");var subQ1=sQuery(id+"F6.wireOp",EDGE,"E126");var subQ2=makeQuery(id+"F6.imprint","INTERSECT",VERTEX,{"disambiguationData":[OD(0.0)],"derivedFrom":[subQ1,subQ0]});Q18=makeQuery(id+"F6.imprint","IMPRINT",FACE,{"disambiguationData":[TD([[makeQuery(id+"F6.imprint","IMPRINT",EDGE,{"disambiguationData":[TD([[subQ2,-1.0]])],"derivedFrom":subQ1}),1.0]])]});}
            var Q19;
            {var subQ0=sQuery(id+"F6.wireOp",EDGE,"E128");var subQ1=sQuery(id+"F6.wireOp",EDGE,"E126");var subQ2=makeQuery(id+"F6.imprint","INTERSECT",VERTEX,{"disambiguationData":[OD(0.0)],"derivedFrom":[subQ1,subQ0]});Q19=makeQuery(id+"F6.imprint","IMPRINT",FACE,{"disambiguationData":[TD([[makeQuery(id+"F6.imprint","IMPRINT",EDGE,{"disambiguationData":[TD([[subQ2,-1.0]])],"derivedFrom":subQ1}),-1.0]])]});}
            var Q20;
            Q20=makeQuery(id+"F6.imprint","IMPRINT",FACE,{"disambiguationData":[TD([[makeQuery(id+"F6.imprint","IMPRINT",EDGE,{"derivedFrom":sQuery(id+"F6.wireOp",EDGE,"E122")}),1.0]])]});
            var Q21;
            {var subQ0=sQuery(id+"F6.wireOp",EDGE,"E134");var subQ1=sQuery(id+"F6.wireOp",EDGE,"E130");var subQ2=makeQuery(id+"F6.imprint","INTERSECT",VERTEX,{"disambiguationData":[OD(0.0)],"derivedFrom":[subQ1,subQ0]});Q21=makeQuery(id+"F6.imprint","IMPRINT",FACE,{"disambiguationData":[TD([[makeQuery(id+"F6.imprint","IMPRINT",EDGE,{"disambiguationData":[TD([[subQ2,-1.0]])],"derivedFrom":subQ1}),1.0]])]});}
            var Q22;
            {var subQ0=sQuery(id+"F6.wireOp",EDGE,"E134");var subQ1=sQuery(id+"F6.wireOp",EDGE,"E130");var subQ2=makeQuery(id+"F6.imprint","INTERSECT",VERTEX,{"disambiguationData":[OD(0.0)],"derivedFrom":[subQ1,subQ0]});Q22=makeQuery(id+"F6.imprint","IMPRINT",FACE,{"disambiguationData":[TD([[makeQuery(id+"F6.imprint","IMPRINT",EDGE,{"disambiguationData":[TD([[subQ2,-1.0]])],"derivedFrom":subQ1}),-1.0]])]});}
            var Q23;
            {var subQ0=sQuery(id+"F6.wireOp",EDGE,"E133");var subQ1=sQuery(id+"F6.wireOp",EDGE,"E130");var subQ2=makeQuery(id+"F6.imprint","INTERSECT",VERTEX,{"disambiguationData":[OD(0.0)],"derivedFrom":[subQ1,subQ0]});Q23=makeQuery(id+"F6.imprint","IMPRINT",FACE,{"disambiguationData":[TD([[makeQuery(id+"F6.imprint","IMPRINT",EDGE,{"disambiguationData":[TD([[subQ2,-1.0]])],"derivedFrom":subQ1}),1.0]])]});}
            var Q24;
            {var subQ0=sQuery(id+"F6.wireOp",EDGE,"E133");var subQ1=sQuery(id+"F6.wireOp",EDGE,"E130");var subQ2=makeQuery(id+"F6.imprint","INTERSECT",VERTEX,{"disambiguationData":[OD(0.0)],"derivedFrom":[subQ1,subQ0]});Q24=makeQuery(id+"F6.imprint","IMPRINT",FACE,{"disambiguationData":[TD([[makeQuery(id+"F6.imprint","IMPRINT",EDGE,{"disambiguationData":[TD([[subQ2,-1.0]])],"derivedFrom":subQ1}),-1.0]])]});}
            extrude(context, id + "F7", {"entities" : qUnion([Q0, Q1, Q2, Q3, Q4, Q5, Q6, Q7, Q8, Q9, Q10, Q11, Q12, Q13, Q14, Q15, Q16, Q17, Q18, Q19, Q20, Q21, Q22, Q23, Q24]), "operationType" : NewBodyOperationType.REMOVE, "oppositeDirection" : true, "depth" : 25.4 * mm});
        }
        {
            var Q0;
            {var subQ0=sQuery(id+"F0.wireOp",EDGE,"E58");var subQ1=sQuery(id+"F0.wireOp",EDGE,"E57");var subQ2=sQuery(id+"F0.wireOp",EDGE,"E56");var subQ3=sQuery(id+"F0.wireOp",EDGE,"E55");var subQ4=sQuery(id+"F0.wireOp",EDGE,"E51");var subQ5=sQuery(id+"F0.wireOp",EDGE,"E50");var subQ6=sQuery(id+"F0.wireOp",EDGE,"E49");Q0=makeQuery(id+"F5.opBoolean","MERGE",FACE,{"derivedFrom":[makeQuery(id+"F1.opExtrude","CAP_FACE",FACE,{"disambiguationData":[OSD([sQuery(id+"F0.wireOp",EDGE,"E0"),sQuery(id+"F0.wireOp",EDGE,"E1"),sQuery(id+"F0.wireOp",EDGE,"E2"),sQuery(id+"F0.wireOp",EDGE,"E3"),sQuery(id+"F0.wireOp",EDGE,"E4"),sQuery(id+"F0.wireOp",EDGE,"E5"),sQuery(id+"F0.wireOp",EDGE,"E6"),sQuery(id+"F0.wireOp",EDGE,"E7"),sQuery(id+"F0.wireOp",EDGE,"E8"),sQuery(id+"F0.wireOp",EDGE,"E9"),sQuery(id+"F0.wireOp",EDGE,"E10"),sQuery(id+"F0.wireOp",EDGE,"E11"),sQuery(id+"F0.wireOp",EDGE,"E12"),sQuery(id+"F0.wireOp",EDGE,"E13"),sQuery(id+"F0.wireOp",EDGE,"E14"),sQuery(id+"F0.wireOp",EDGE,"E15"),sQuery(id+"F0.wireOp",EDGE,"E31"),sQuery(id+"F0.wireOp",EDGE,"E32"),sQuery(id+"F0.wireOp",EDGE,"E33"),sQuery(id+"F0.wireOp",EDGE,"E34"),sQuery(id+"F0.wireOp",EDGE,"E35"),sQuery(id+"F0.wireOp",EDGE,"E36"),sQuery(id+"F0.wireOp",EDGE,"E37"),sQuery(id+"F0.wireOp",EDGE,"E38"),sQuery(id+"F0.wireOp",EDGE,"E39"),sQuery(id+"F0.wireOp",EDGE,"E40"),sQuery(id+"F0.wireOp",EDGE,"E41"),sQuery(id+"F0.wireOp",EDGE,"E42"),sQuery(id+"F0.wireOp",EDGE,"E43"),sQuery(id+"F0.wireOp",EDGE,"E44"),sQuery(id+"F0.wireOp",EDGE,"E45"),sQuery(id+"F0.wireOp",EDGE,"E46"),sQuery(id+"F0.wireOp",EDGE,"E48"),subQ6,subQ5,subQ4,sQuery(id+"F0.wireOp",EDGE,"JAnZBrHo-FBBG-eloX-0JCn-rR0iuovSbzPm"),sQuery(id+"F0.wireOp",EDGE,"E52"),sQuery(id+"F0.wireOp",EDGE,"E53"),sQuery(id+"F0.wireOp",EDGE,"E54"),subQ3,subQ2,subQ1,subQ0,sQuery(id+"F0.wireOp",EDGE,"E61"),sQuery(id+"F0.wireOp",EDGE,"E62")])],"isStart":false}),makeQuery(id+"F2.opExtrude","CAP_FACE",FACE,{"disambiguationData":[OSD([subQ6,subQ5,subQ4,subQ3,subQ2,subQ1,subQ0,sQuery(id+"F0.wireOp",EDGE,"E59"),sQuery(id+"F0.wireOp",EDGE,"E60")])],"isStart":false})]});}
            var sketch = newSketch(context, id + "F8", { "sketchPlane" : qUnion([Q0])});
            skPoint(sketch, "E135", {"position": v(-1.6, -25.6) * mm});
            skPoint(sketch, "E136", {"position": v(-1.6, 22.03) * mm});
            skLineSegment(sketch, "E137", {"start": v(-1.6, -25.6) * mm, "end": v(-1.6, 22.03) * mm});
            skCircle(sketch, "E138", {"center": v(-1.6, 22.03) * mm, "radius": 2.38 * mm});
            skCircle(sketch, "E139", {"center": v(-1.6, -25.6) * mm, "radius": 2.38 * mm});
            skSolve(sketch);
        }
        {
            var Q0;
            Q0 = qSketchRegion(id + "F8", true);
            extrude(context, id + "F9", {"entities" : qUnion([Q0]), "operationType" : NewBodyOperationType.REMOVE, "oppositeDirection" : true, "depth" : 25.4 * mm});
        }
    });
